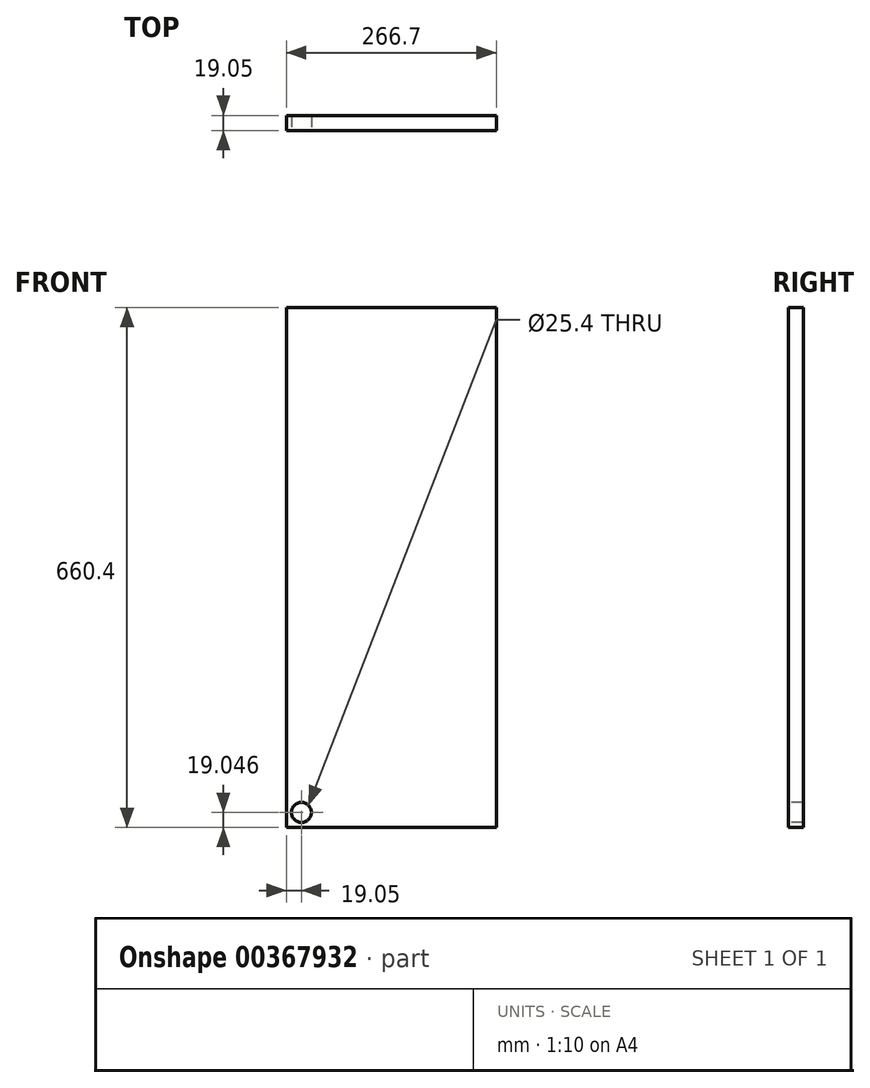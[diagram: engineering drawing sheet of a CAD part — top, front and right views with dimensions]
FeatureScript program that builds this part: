
annotation { "Feature Type Name" : "Feature", "Feature Type Description" : "" }
export const myFeature = defineFeature(function(context is Context, id is Id, definition is map)
    precondition{}
    {
        {
            var Q0;
            Q0=qCreatedBy(makeId("Front.planeOp"),FACE);
            var sketch = newSketch(context, id + "F0", { "sketchPlane" : qUnion([Q0])});
            skLineSegment(sketch, "E0.bottom", {"start": v(-19.05, 637.6) * mm, "end": v(247.65, 637.6) * mm});
            skLineSegment(sketch, "E0.top", {"start": v(-19.05, -22.8) * mm, "end": v(247.65, -22.8) * mm});
            skLineSegment(sketch, "E0.left", {"start": v(-19.05, 637.6) * mm, "end": v(-19.05, -22.8) * mm});
            skLineSegment(sketch, "E0.right", {"start": v(247.65, 637.6) * mm, "end": v(247.65, -22.8) * mm});
            skPoint(sketch, "E1", {"position": v(0, -3.75) * mm});
            skSolve(sketch);
        }
        {
            var Q0;
            Q0=makeQuery(id+"F0.imprint","IMPRINT",FACE,{"disambiguationData":[TD([[makeQuery(id+"F0.imprint","IMPRINT",EDGE,{"derivedFrom":sQuery(id+"F0.wireOp",EDGE,"E0.bottom")}),-1.0]])]});
            extrude(context, id + "F1", {"entities" : qUnion([Q0]), "depth" : 19.05 * mm});
        }
        {
            var Q0;
            Q0=sQuery(id+"F0.wireOp",VERTEX,"E1");
            var Q1;
            Q1=makeQuery(id+"F1.opExtrude","SWEPT_BODY",BODY,{"disambiguationData":[OSD([sQuery(id+"F0.wireOp",EDGE,"E0.bottom"),sQuery(id+"F0.wireOp",EDGE,"E0.top"),sQuery(id+"F0.wireOp",EDGE,"E0.left"),sQuery(id+"F0.wireOp",EDGE,"E0.right")])]});
            hole(context, id + "F2", {"style" : HoleStyle.SIMPLE, "endStyle" : HoleEndStyle.THROUGH, "oppositeDirection" : true, "holeDiameter" : 25.4 * mm, "isTappedThrough" : true, "tappedDepth" : 12.7 * mm, "tapClearance" : 3, "locations" : qUnion([Q0]), "scope" : qUnion([Q1])});
        }
    });
